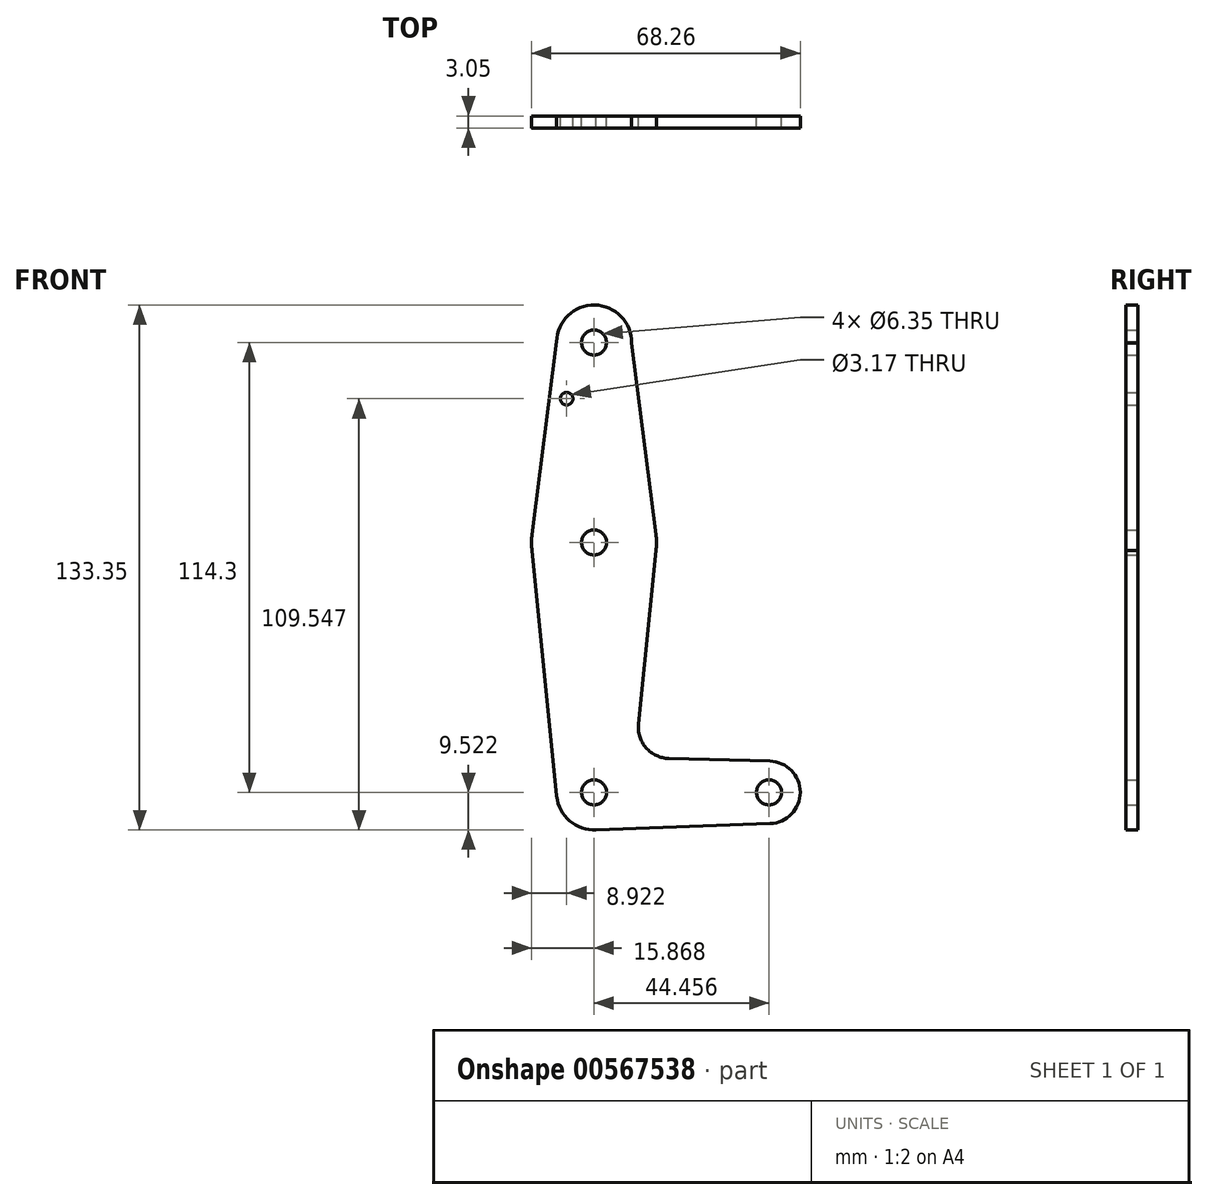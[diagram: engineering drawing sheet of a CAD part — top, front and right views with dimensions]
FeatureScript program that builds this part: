
annotation { "Feature Type Name" : "Feature", "Feature Type Description" : "" }
export const myFeature = defineFeature(function(context is Context, id is Id, definition is map)
    precondition{}
    {
        {
            var Q0;
            Q0=qCreatedBy(makeId("Front.planeOp"),FACE);
            var sketch = newSketch(context, id + "F0", { "sketchPlane" : qUnion([Q0])});
            skCircle(sketch, "E0", {"center": v(-18.3, -12.84) * mm, "radius": 9.53 * mm});
            skCircle(sketch, "E1", {"center": v(26.14, -12.84) * mm, "radius": 7.94 * mm});
            skCircle(sketch, "E2", {"center": v(-18.3, 50.66) * mm, "radius": 15.88 * mm});
            skCircle(sketch, "E3", {"center": v(-18.31, 101.46) * mm, "radius": 9.53 * mm});
            skLineSegment(sketch, "E4", {"start": v(-18.31, 101.46) * mm, "end": v(-18.3, -12.84) * mm, "construction": true});
            skLineSegment(sketch, "E5", {"start": v(-18.3, -12.84) * mm, "end": v(26.14, -12.84) * mm, "construction": true});
            skLineSegment(sketch, "E6", {"start": v(-27.83, 101.68) * mm, "end": v(-34.05, 52.66) * mm});
            skLineSegment(sketch, "E7", {"start": v(-34.05, 52.66) * mm, "end": v(-34.05, 48.66) * mm});
            skLineSegment(sketch, "E8", {"start": v(-34.05, 48.66) * mm, "end": v(-27.78, -13.79) * mm});
            skLineSegment(sketch, "E9", {"start": v(-8.79, 101.31) * mm, "end": v(-2.56, 52.68) * mm});
            skLineSegment(sketch, "E10", {"start": v(-2.56, 52.68) * mm, "end": v(-2.56, 48.65) * mm});
            skLineSegment(sketch, "E11", {"start": v(-2.56, 48.65) * mm, "end": v(-7.02, 4.53) * mm});
            skLineSegment(sketch, "E12", {"start": v(-18.19, -22.36) * mm, "end": v(26.43, -20.77) * mm});
            skLineSegment(sketch, "E13", {"start": v(0.67, -4.22) * mm, "end": v(26.36, -4.9) * mm});
            skCircle(sketch, "E14", {"center": v(-18.31, 101.46) * mm, "radius": 3.18 * mm});
            skCircle(sketch, "E15", {"center": v(-18.3, 50.66) * mm, "radius": 3.18 * mm});
            skCircle(sketch, "E16", {"center": v(-18.3, -12.84) * mm, "radius": 3.18 * mm});
            skCircle(sketch, "E17", {"center": v(26.14, -12.84) * mm, "radius": 3.18 * mm});
            skCircle(sketch, "E18", {"center": v(-25.26, 87.19) * mm, "radius": 1.59 * mm});
            skArc(sketch, "E19.filletArc", {"start": v(-7.02, 4.53) * mm, "mid": v(-5.08, -1.52) * mm, "end": v(0.67, -4.22) * mm});
            skSolve(sketch);
        }
        {
            var Q0;
            Q0 = qSketchRegion(id + "F0", true);
            extrude(context, id + "F1", {"entities" : qUnion([Q0]), "depth" : 3.05 * mm, "offsetDistance" : 25.4 * mm});
        }
    });
